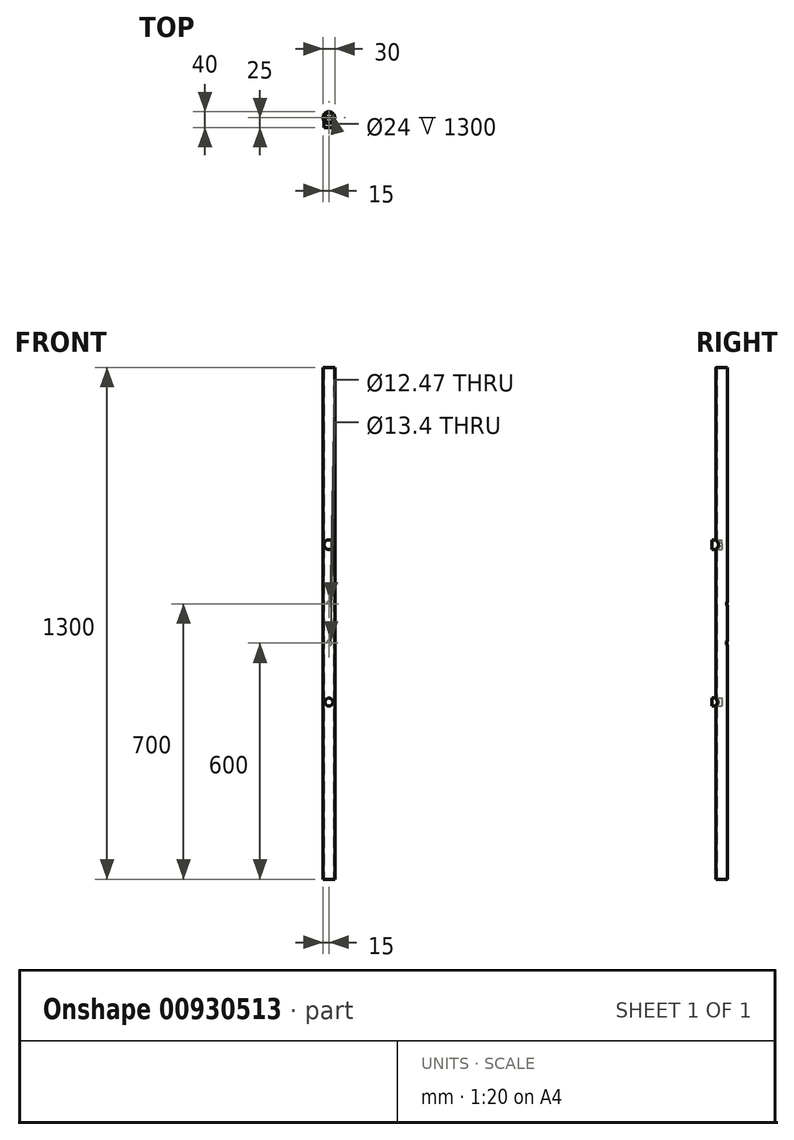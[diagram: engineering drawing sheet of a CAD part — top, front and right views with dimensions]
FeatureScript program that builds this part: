
annotation { "Feature Type Name" : "Feature", "Feature Type Description" : "" }
export const myFeature = defineFeature(function(context is Context, id is Id, definition is map)
    precondition{}
    {
        {
            var Q0;
            Q0=qCreatedBy(makeId("Top.planeOp"),FACE);
            var sketch = newSketch(context, id + "F0", { "sketchPlane" : qUnion([Q0])});
            skCircle(sketch, "E0", {"center": v(0, 0) * mm, "radius": 15 * mm});
            skCircle(sketch, "E1", {"center": v(0, 0) * mm, "radius": 12 * mm});
            skSolve(sketch);
        }
        {
            var Q0;
            Q0 = qSketchRegion(id + "F0", true);
            extrude(context, id + "F1", {"entities" : qUnion([Q0]), "depth" : 1300 * mm, "offsetDistance" : 25 * mm});
        }
        {
            var Q0;
            Q0=qCreatedBy(makeId("Front.planeOp"),FACE);
            var sketch = newSketch(context, id + "F2", { "sketchPlane" : qUnion([Q0])});
            skCircle(sketch, "E2", {"center": v(0, 600) * mm, "radius": 6.7 * mm});
            skCircle(sketch, "E3", {"center": v(0, 700) * mm, "radius": 6.24 * mm});
            skSolve(sketch);
        }
        {
            var Q0;
            Q0 = qSketchRegion(id + "F2", true);
            extrude(context, id + "F3", {"entities" : qUnion([Q0]), "operationType" : NewBodyOperationType.REMOVE, "oppositeDirection" : true, "depth" : 25 * mm, "offsetDistance" : 25 * mm});
        }
        {
            var Q0;
            Q0=qCreatedBy(makeId("Front.planeOp"),FACE);
            var sketch = newSketch(context, id + "F4", { "sketchPlane" : qUnion([Q0])});
            skCircle(sketch, "E4", {"center": v(0, 450) * mm, "radius": 10 * mm});
            skCircle(sketch, "E5", {"center": v(0, 850) * mm, "radius": 12.5 * mm});
            skSolve(sketch);
        }
        {
            var Q0;
            Q0 = qSketchRegion(id + "F4", true);
            extrude(context, id + "F5", {"entities" : qUnion([Q0]), "operationType" : NewBodyOperationType.ADD, "depth" : 25 * mm, "offsetDistance" : 25 * mm});
        }
    });
